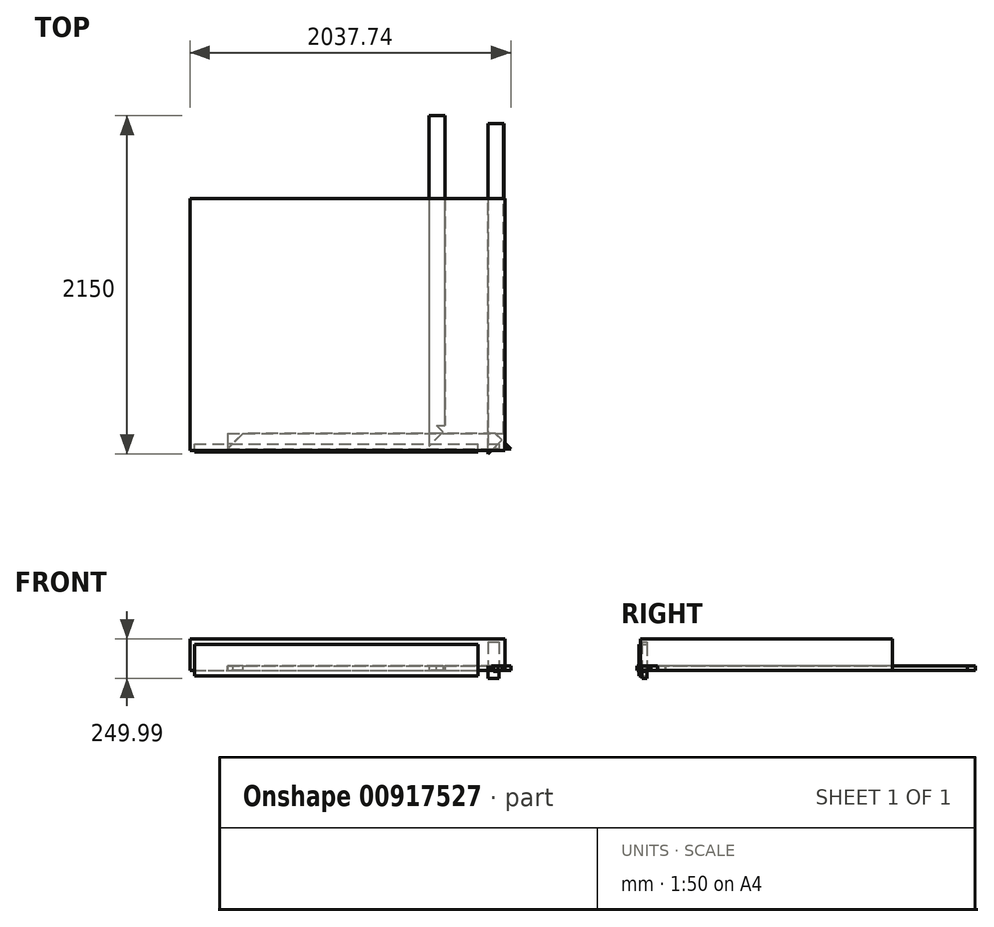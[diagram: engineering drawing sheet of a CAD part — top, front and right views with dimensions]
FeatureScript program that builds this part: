
annotation { "Feature Type Name" : "Feature", "Feature Type Description" : "" }
export const myFeature = defineFeature(function(context is Context, id is Id, definition is map)
    precondition{}
    {
        {
            var Q0;
            Q0=qCreatedBy(makeId("Front.planeOp"),FACE);
            var sketch = newSketch(context, id + "F0", { "sketchPlane" : qUnion([Q0])});
            skLineSegment(sketch, "E0.bottom", {"start": v(-1914.26, 166.7) * mm, "end": v(-114.26, 166.7) * mm});
            skLineSegment(sketch, "E0.top", {"start": v(-1914.26, -33.3) * mm, "end": v(-114.26, -33.3) * mm});
            skLineSegment(sketch, "E0.left", {"start": v(-1914.26, 166.7) * mm, "end": v(-1914.26, -33.3) * mm});
            skLineSegment(sketch, "E0.right", {"start": v(-114.26, 166.7) * mm, "end": v(-114.26, -33.3) * mm});
            skSolve(sketch);
        }
        {
            var Q0;
            Q0=qSketchRegion(id+"F0",true);
            extrude(context, id + "F1", {"entities" : qUnion([Q0]), "depth" : 50 * mm, "offsetDistance" : 25 * mm});
        }
        {
            var Q0;
            Q0=qCreatedBy(makeId("Top.planeOp"),FACE);
            var sketch = newSketch(context, id + "F2", { "sketchPlane" : qUnion([Q0])});
            skLineSegment(sketch, "E1.bottom", {"start": v(-49.26, 2036.58) * mm, "end": v(50.74, 2036.58) * mm});
            skLineSegment(sketch, "E1.top", {"start": v(-49.26, -63.42) * mm, "end": v(50.74, -63.42) * mm});
            skLineSegment(sketch, "E1.left", {"start": v(-49.26, 2036.58) * mm, "end": v(-49.26, -63.42) * mm});
            skLineSegment(sketch, "E1.right", {"start": v(50.74, 2036.58) * mm, "end": v(50.74, -63.42) * mm});
            skSolve(sketch);
        }
        {
            var Q0;
            Q0=qSketchRegion(id+"F2",true);
            extrude(context, id + "F3", {"entities" : qUnion([Q0]), "depth" : 30 * mm, "offsetDistance" : 25 * mm});
        }
        {
            var Q0;
            Q0=qCreatedBy(makeId("Front.planeOp"),FACE);
            var sketch = newSketch(context, id + "F4", { "sketchPlane" : qUnion([Q0])});
            skLineSegment(sketch, "E2.bottom", {"start": v(-49.26, 180.01) * mm, "end": v(20.74, 180.01) * mm});
            skLineSegment(sketch, "E2.top", {"start": v(-49.26, -49.99) * mm, "end": v(20.74, -49.99) * mm});
            skLineSegment(sketch, "E2.left", {"start": v(-49.26, 180.01) * mm, "end": v(-49.26, -49.99) * mm});
            skLineSegment(sketch, "E2.right", {"start": v(20.74, 180.01) * mm, "end": v(20.74, -49.99) * mm});
            skSolve(sketch);
        }
        {
            var Q0;
            Q0=qSketchRegion(id+"F4",true);
            extrude(context, id + "F5", {"entities" : qUnion([Q0]), "depth" : 30 * mm, "offsetDistance" : 25 * mm});
        }
        {
            var Q0;
            Q0=qCreatedBy(makeId("Top.planeOp"),FACE);
            var sketch = newSketch(context, id + "F6", { "sketchPlane" : qUnion([Q0])});
            skLineSegment(sketch, "E3.bottom", {"start": v(-1941.66, 1559.63) * mm, "end": v(58.34, 1559.63) * mm});
            skLineSegment(sketch, "E3.top", {"start": v(-1941.66, -40.37) * mm, "end": v(58.34, -40.37) * mm});
            skLineSegment(sketch, "E3.left", {"start": v(-1941.66, 1559.63) * mm, "end": v(-1941.66, -40.37) * mm});
            skLineSegment(sketch, "E3.right", {"start": v(58.34, 1559.63) * mm, "end": v(58.34, -40.37) * mm});
            skSolve(sketch);
        }
        {
            var Q0;
            Q0=qSketchRegion(id+"F6",true);
            extrude(context, id + "F7", {"entities" : qUnion([Q0]), "depth" : 200 * mm, "offsetDistance" : 25 * mm});
        }
        {
            var Q0;
            Q0=qCreatedBy(makeId("Top.planeOp"),FACE);
            var sketch = newSketch(context, id + "F8", { "sketchPlane" : qUnion([Q0])});
            skLineSegment(sketch, "E4.bottom", {"start": v(-1703.92, 68.52) * mm, "end": v(96.08, 68.52) * mm});
            skLineSegment(sketch, "E4.top", {"start": v(-1703.92, -31.48) * mm, "end": v(96.08, -31.48) * mm});
            skLineSegment(sketch, "E4.left", {"start": v(-1703.92, 68.52) * mm, "end": v(-1703.92, -31.48) * mm});
            skLineSegment(sketch, "E4.right", {"start": v(96.08, 68.52) * mm, "end": v(96.08, -31.48) * mm});
            skSolve(sketch);
        }
        {
            var Q0;
            Q0 = qSketchRegion(id + "F8", true);
            extrude(context, id + "F9", {"entities" : qUnion([Q0]), "depth" : 30 * mm, "offsetDistance" : 25 * mm});
        }
        {
            var Q0;
            Q0=makeQuery(id+"F9.opExtrude","CAP_FACE",FACE,{"disambiguationData":[OSD([sQuery(id+"F8.wireOp",EDGE,"E4.bottom"),sQuery(id+"F8.wireOp",EDGE,"E4.top"),sQuery(id+"F8.wireOp",EDGE,"E4.left"),sQuery(id+"F8.wireOp",EDGE,"E4.right")])],"isStart":false});
            var sketch = newSketch(context, id + "F10", { "sketchPlane" : qUnion([Q0])});
            skLineSegment(sketch, "E5", {"start": v(-1603.92, 68.52) * mm, "end": v(-1703.92, -31.48) * mm});
            skLineSegment(sketch, "E6", {"start": v(-1703.92, -31.48) * mm, "end": v(-1703.92, 63.03) * mm});
            skLineSegment(sketch, "E7", {"start": v(-1703.92, 63.03) * mm, "end": v(-1703.92, 68.52) * mm});
            skLineSegment(sketch, "E8", {"start": v(-1703.92, 68.52) * mm, "end": v(-1603.92, 68.52) * mm});
            skLineSegment(sketch, "E9", {"start": v(-3.92, 68.52) * mm, "end": v(96.08, -31.48) * mm});
            skLineSegment(sketch, "E10", {"start": v(96.08, -31.48) * mm, "end": v(96.08, 68.52) * mm});
            skLineSegment(sketch, "E11", {"start": v(96.08, 68.52) * mm, "end": v(-3.92, 68.52) * mm});
            skSolve(sketch);
        }
        {
            var Q0;
            Q0 = qSketchRegion(id + "F10", true);
            extrude(context, id + "F11", {"entities" : qUnion([Q0]), "operationType" : NewBodyOperationType.REMOVE, "oppositeDirection" : true, "depth" : 34 * mm, "offsetDistance" : 25 * mm});
        }
        {
            var Q0;
            Q0=makeQuery(id+"F11.boolean.opBoolean","COPY",EDGE,{"derivedFrom":makeQuery(id+"F11.opExtrude","CAP_EDGE",EDGE,{"disambiguationData":[OSD([sQuery(id+"F10.wireOp",EDGE,"E5")])],"isStart":true})});
            var Q1;
            Q1=makeQuery(id+"F11.boolean.opBoolean","COPY",EDGE,{"derivedFrom":makeQuery(id+"F11.opExtrude","CAP_EDGE",EDGE,{"disambiguationData":[OSD([sQuery(id+"F10.wireOp",EDGE,"E9")])],"isStart":true})});
            chamfer(context, id + "F12", {"entities" : qUnion([Q0, Q1]), "width" : 1 * mm, "tangentPropagation" : true});
        }
        {
            var Q0;
            Q0=makeQuery(id+"F9.opExtrude","CAP_EDGE",EDGE,{"disambiguationData":[OSD([sQuery(id+"F8.wireOp",EDGE,"E4.bottom")])],"isStart":false});
            chamfer(context, id + "F13", {"entities" : qUnion([Q0]), "width" : 1 * mm, "tangentPropagation" : true});
        }
        {
            var Q0;
            Q0=makeQuery(id+"F9.opExtrude","CAP_EDGE",EDGE,{"disambiguationData":[OSD([sQuery(id+"F8.wireOp",EDGE,"E4.top")])],"isStart":false});
            chamfer(context, id + "F14", {"entities" : qUnion([Q0]), "width" : 1 * mm, "tangentPropagation" : true});
        }
        {
            var Q0;
            Q0=makeQuery(id+"F3.opExtrude","CAP_FACE",FACE,{"disambiguationData":[OSD([sQuery(id+"F2.wireOp",EDGE,"E1.bottom"),sQuery(id+"F2.wireOp",EDGE,"E1.top"),sQuery(id+"F2.wireOp",EDGE,"E1.left"),sQuery(id+"F2.wireOp",EDGE,"E1.right")])],"isStart":false});
            var sketch = newSketch(context, id + "F15", { "sketchPlane" : qUnion([Q0])});
            skLineSegment(sketch, "E12", {"start": v(50.74, 36.58) * mm, "end": v(-49.26, -63.42) * mm});
            skLineSegment(sketch, "E13", {"start": v(-49.26, -63.42) * mm, "end": v(50.74, -63.42) * mm});
            skLineSegment(sketch, "E14", {"start": v(50.74, -63.42) * mm, "end": v(50.74, 36.58) * mm});
            skSolve(sketch);
        }
        {
            var Q0;
            Q0 = qSketchRegion(id + "F15", true);
            extrude(context, id + "F16", {"entities" : qUnion([Q0]), "operationType" : NewBodyOperationType.REMOVE, "oppositeDirection" : true, "depth" : 35 * mm, "offsetDistance" : 25 * mm});
        }
        {
            var Q0;
            Q0=makeQuery(id+"F3.opExtrude","SWEPT_BODY",BODY,{"disambiguationData":[OSD([sQuery(id+"F2.wireOp",EDGE,"E1.bottom"),sQuery(id+"F2.wireOp",EDGE,"E1.top"),sQuery(id+"F2.wireOp",EDGE,"E1.left"),sQuery(id+"F2.wireOp",EDGE,"E1.right")])]});
            transform(context, id + "F17", {"entities" : qUnion([Q0]), "transformType" : TransformType.TRANSLATION_3D, "dx" : -374 * mm, "dy" : 50 * mm, "dz" : 0 * mm, "makeCopy" : true});
        }
        {
            var Q0;
            Q0=makeQuery(id+"F3.opExtrude","CAP_EDGE",EDGE,{"disambiguationData":[OSD([sQuery(id+"F2.wireOp",EDGE,"E1.right")])],"isStart":false});
            var Q1;
            Q1=makeQuery(id+"F16.boolean.opBoolean","COPY",EDGE,{"derivedFrom":makeQuery(id+"F16.opExtrude","CAP_EDGE",EDGE,{"disambiguationData":[OSD([sQuery(id+"F15.wireOp",EDGE,"E12")])],"isStart":true})});
            chamfer(context, id + "F18", {"entities" : qUnion([Q0, Q1]), "width" : 1 * mm, "tangentPropagation" : true});
        }
        {
            var Q0;
            Q0=makeQuery(id+"F3.opExtrude","CAP_EDGE",EDGE,{"disambiguationData":[OSD([sQuery(id+"F2.wireOp",EDGE,"E1.left")])],"isStart":false});
            var Q1;
            Q1=makeQuery(id+"F3.opExtrude","CAP_EDGE",EDGE,{"disambiguationData":[OSD([sQuery(id+"F2.wireOp",EDGE,"E1.bottom")])],"isStart":false});
            chamfer(context, id + "F19", {"entities" : qUnion([Q0, Q1]), "width" : 1 * mm, "tangentPropagation" : true});
        }
        {
            var Q0;
            Q0=makeQuery(id+"F17.opPattern","COPY",EDGE,{"derivedFrom":makeQuery(id+"F16.boolean.opBoolean","INTERSECT",EDGE,{"derivedFrom":[makeQuery(id+"F3.opExtrude","CAP_FACE",FACE,{"disambiguationData":[OSD([sQuery(id+"F2.wireOp",EDGE,"E1.bottom"),sQuery(id+"F2.wireOp",EDGE,"E1.top"),sQuery(id+"F2.wireOp",EDGE,"E1.left"),sQuery(id+"F2.wireOp",EDGE,"E1.right")])],"isStart":true}),makeQuery(id+"F16.opExtrude","SWEPT_FACE",FACE,{"disambiguationData":[OSD([sQuery(id+"F15.wireOp",EDGE,"E12")])]})]}),"instanceName":"1"});
            var Q1;
            Q1=makeQuery(id+"F17.opPattern","COPY",EDGE,{"derivedFrom":makeQuery(id+"F3.opExtrude","CAP_EDGE",EDGE,{"disambiguationData":[OSD([sQuery(id+"F2.wireOp",EDGE,"E1.right")])],"isStart":true}),"instanceName":"1"});
            chamfer(context, id + "F20", {"entities" : qUnion([Q0, Q1]), "width" : 1 * mm, "tangentPropagation" : true});
        }
        {
            var Q0;
            Q0=makeQuery(id+"F17.opPattern","COPY",EDGE,{"derivedFrom":makeQuery(id+"F3.opExtrude","CAP_EDGE",EDGE,{"disambiguationData":[OSD([sQuery(id+"F2.wireOp",EDGE,"E1.bottom")])],"isStart":true}),"instanceName":"1"});
            var Q1;
            Q1=makeQuery(id+"F17.opPattern","COPY",EDGE,{"derivedFrom":makeQuery(id+"F3.opExtrude","CAP_EDGE",EDGE,{"disambiguationData":[OSD([sQuery(id+"F2.wireOp",EDGE,"E1.left")])],"isStart":true}),"instanceName":"1"});
            chamfer(context, id + "F21", {"entities" : qUnion([Q0, Q1]), "width" : 1 * mm, "tangentPropagation" : true});
        }
    });
